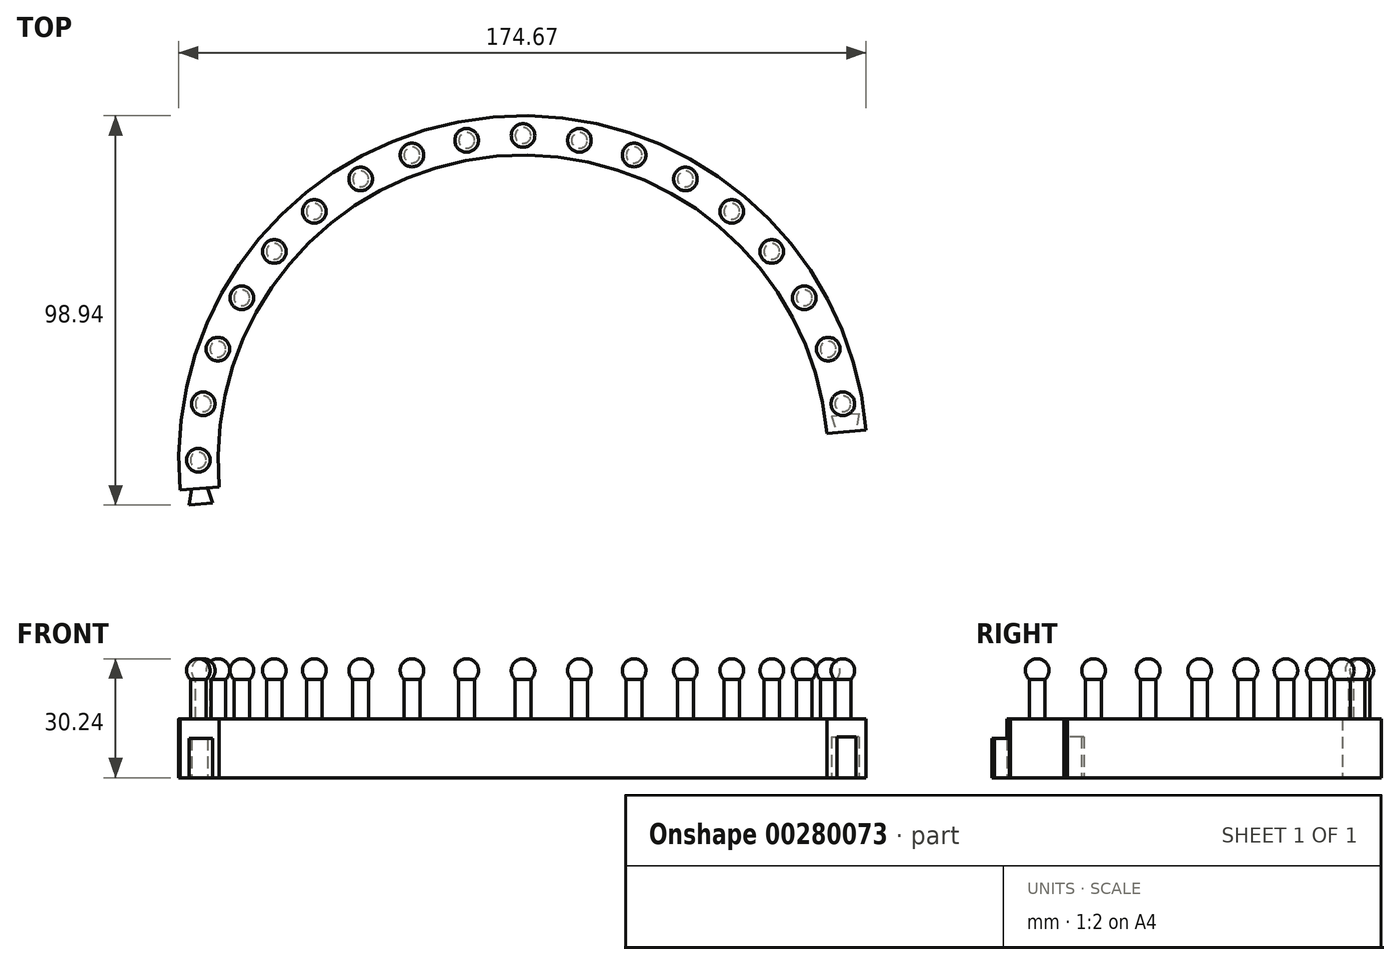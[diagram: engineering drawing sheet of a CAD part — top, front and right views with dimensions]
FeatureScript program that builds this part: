
annotation { "Feature Type Name" : "Feature", "Feature Type Description" : "" }
export const myFeature = defineFeature(function(context is Context, id is Id, definition is map)
    precondition{}
    {
        {
            var Q0;
            Q0=qCreatedBy(makeId("Top.planeOp"),FACE);
            var sketch = newSketch(context, id + "F0", { "sketchPlane" : qUnion([Q0])});
            skCircle(sketch, "E0", {"center": v(0, 0) * mm, "radius": 77.5 * mm});
            skCircle(sketch, "E1", {"center": v(0, 0) * mm, "radius": 87.5 * mm});
            skSolve(sketch);
        }
        {
            var Q0;
            Q0 = qSketchRegion(id + "F0", true);
            extrude(context, id + "F1", {"entities" : qUnion([Q0]), "depth" : 15 * mm});
        }
        {
            var Q0;
            Q0=qCreatedBy(makeId("Front.planeOp"),FACE);
            var sketch = newSketch(context, id + "F2", { "sketchPlane" : qUnion([Q0])});
            skLineSegment(sketch, "E2", {"start": v(-80.5, 15) * mm, "end": v(-80.5, 25) * mm});
            skArc(sketch, "E3", {"start": v(-80.5, 25) * mm, "mid": v(-79.7, 28.3) * mm, "end": v(-82.5, 30.24) * mm});
            skLineSegment(sketch, "E4", {"start": v(-82.5, 30.24) * mm, "end": v(-82.5, 15) * mm});
            skLineSegment(sketch, "E5", {"start": v(-82.5, 15) * mm, "end": v(-80.5, 15) * mm});
            skPoint(sketch, "E6", {"position": v(-87.5, 15) * mm});
            skSolve(sketch);
        }
        {
            var Q0;
            Q0=makeQuery(id+"F2.imprint","IMPRINT",FACE,{"disambiguationData":[TD([[makeQuery(id+"F2.imprint","IMPRINT",EDGE,{"derivedFrom":sQuery(id+"F2.wireOp",EDGE,"E2")}),1.0]])]});
            var Q1;
            Q1=sQuery(id+"F2.wireOp",EDGE,"E4");
            var Q2;
            Q2=sQuery(id+"F2.wireOp",EDGE,"E4");
            revolve(context, id + "F3", {"entities" : qUnion([Q0]), "surfaceEntities" : qUnion([Q1]), "axis" : qUnion([Q2]), "revolveType" : RevolveType.FULL});
        }
        {
            var Q0;
            Q0=makeQuery(id+"F3.opRevolve","SWEPT_BODY",BODY,{"disambiguationData":[OSD([sQuery(id+"F2.wireOp",EDGE,"E2"),sQuery(id+"F2.wireOp",EDGE,"E3"),sQuery(id+"F2.wireOp",EDGE,"E4"),sQuery(id+"F2.wireOp",EDGE,"E5")])]});
            var Q1;
            Q1=makeQuery(id+"F1.opExtrude","CAP_EDGE",EDGE,{"disambiguationData":[OSD([sQuery(id+"F0.wireOp",EDGE,"E0")])],"isStart":false});
            circularPattern(context, id + "F4", {"operationType" : NewBodyOperationType.ADD, "entities" : qUnion([Q0]), "axis" : qUnion([Q1]), "angle" : 360 * degree, "instanceCount" : 36, "equalSpace" : true});
        }
        {
            var Q0;
            Q0=qCreatedBy(makeId("Top.planeOp"),FACE);
            var sketch = newSketch(context, id + "F5", { "sketchPlane" : qUnion([Q0])});
            skLineSegment(sketch, "E7", {"start": v(-95.4, -8.35) * mm, "end": v(95.4, 8.35) * mm});
            skLineSegment(sketch, "E8", {"start": v(-95.4, -8.35) * mm, "end": v(-95.4, -98.17) * mm});
            skLineSegment(sketch, "E9", {"start": v(-95.4, -98.17) * mm, "end": v(95.4, -98.17) * mm});
            skLineSegment(sketch, "E10", {"start": v(95.4, -98.17) * mm, "end": v(95.4, 8.35) * mm});
            skSolve(sketch);
        }
        {
            var Q0;
            Q0 = qSketchRegion(id + "F5", true);
            extrude(context, id + "F6", {"entities" : qUnion([Q0]), "operationType" : NewBodyOperationType.REMOVE, "endBound" : BoundingType.THROUGH_ALL, "depth" : 25 * mm});
        }
        {
            var Q0;
            Q0=qCreatedBy(makeId("Top.planeOp"),FACE);
            var sketch = newSketch(context, id + "F7", { "sketchPlane" : qUnion([Q0])});
            skLineSegment(sketch, "E11", {"start": v(-82.19, -7.2) * mm, "end": v(-81.84, -11.18) * mm, "construction": true});
            skLineSegment(sketch, "E12", {"start": v(-80.2, -7.02) * mm, "end": v(-78.85, -10.91) * mm});
            skLineSegment(sketch, "E13", {"start": v(-78.85, -10.91) * mm, "end": v(-81.84, -11.18) * mm});
            skLineSegment(sketch, "E14", {"start": v(-82.19, -7.2) * mm, "end": v(-80.2, -7.02) * mm});
            skLineSegment(sketch, "E15.MirrorCS", {"start": v(-82.19, -7.2) * mm, "end": v(-84.18, -7.36) * mm});
            skLineSegment(sketch, "E16.MirrorCS", {"start": v(-84.18, -7.36) * mm, "end": v(-84.83, -11.44) * mm});
            skLineSegment(sketch, "E17.MirrorCS", {"start": v(-84.83, -11.44) * mm, "end": v(-81.84, -11.18) * mm});
            skSolve(sketch);
        }
        {
            var Q0;
            Q0 = qSketchRegion(id + "F7", true);
            extrude(context, id + "F8", {"entities" : qUnion([Q0]), "operationType" : NewBodyOperationType.ADD, "depth" : 10 * mm});
        }
        {
            var Q0;
            Q0=qCreatedBy(makeId("Top.planeOp"),FACE);
            var sketch = newSketch(context, id + "F9", { "sketchPlane" : qUnion([Q0])});
            skLineSegment(sketch, "E18", {"start": v(82.19, 7.2) * mm, "end": v(81.84, 11.18) * mm, "construction": true});
            skLineSegment(sketch, "E19", {"start": v(81.84, 11.18) * mm, "end": v(84.83, 11.44) * mm, "construction": true});
            skLineSegment(sketch, "E20", {"start": v(84.83, 11.44) * mm, "end": v(84.18, 7.36) * mm, "construction": true});
            skLineSegment(sketch, "E21", {"start": v(84.18, 7.36) * mm, "end": v(82.19, 7.2) * mm});
            skLineSegment(sketch, "E22.0", {"start": v(85.3, 11.88) * mm, "end": v(84.59, 7.4) * mm});
            skLineSegment(sketch, "E22.1", {"start": v(81.8, 11.57) * mm, "end": v(85.3, 11.88) * mm});
            skLineSegment(sketch, "E23", {"start": v(84.18, 7.36) * mm, "end": v(84.59, 7.4) * mm});
            skLineSegment(sketch, "E24.MirrorCS", {"start": v(81.8, 11.57) * mm, "end": v(78.3, 11.27) * mm});
            skLineSegment(sketch, "E25.MirrorCS", {"start": v(78.3, 11.27) * mm, "end": v(79.78, 6.98) * mm});
            skLineSegment(sketch, "E26.MirrorCS", {"start": v(80.2, 7.02) * mm, "end": v(79.78, 6.98) * mm});
            skLineSegment(sketch, "E27.MirrorCS", {"start": v(80.2, 7.02) * mm, "end": v(82.19, 7.2) * mm});
            skSolve(sketch);
        }
        {
            var Q0;
            Q0 = qSketchRegion(id + "F9", true);
            extrude(context, id + "F10", {"entities" : qUnion([Q0]), "operationType" : NewBodyOperationType.REMOVE, "depth" : 10.4 * mm});
        }
    });
